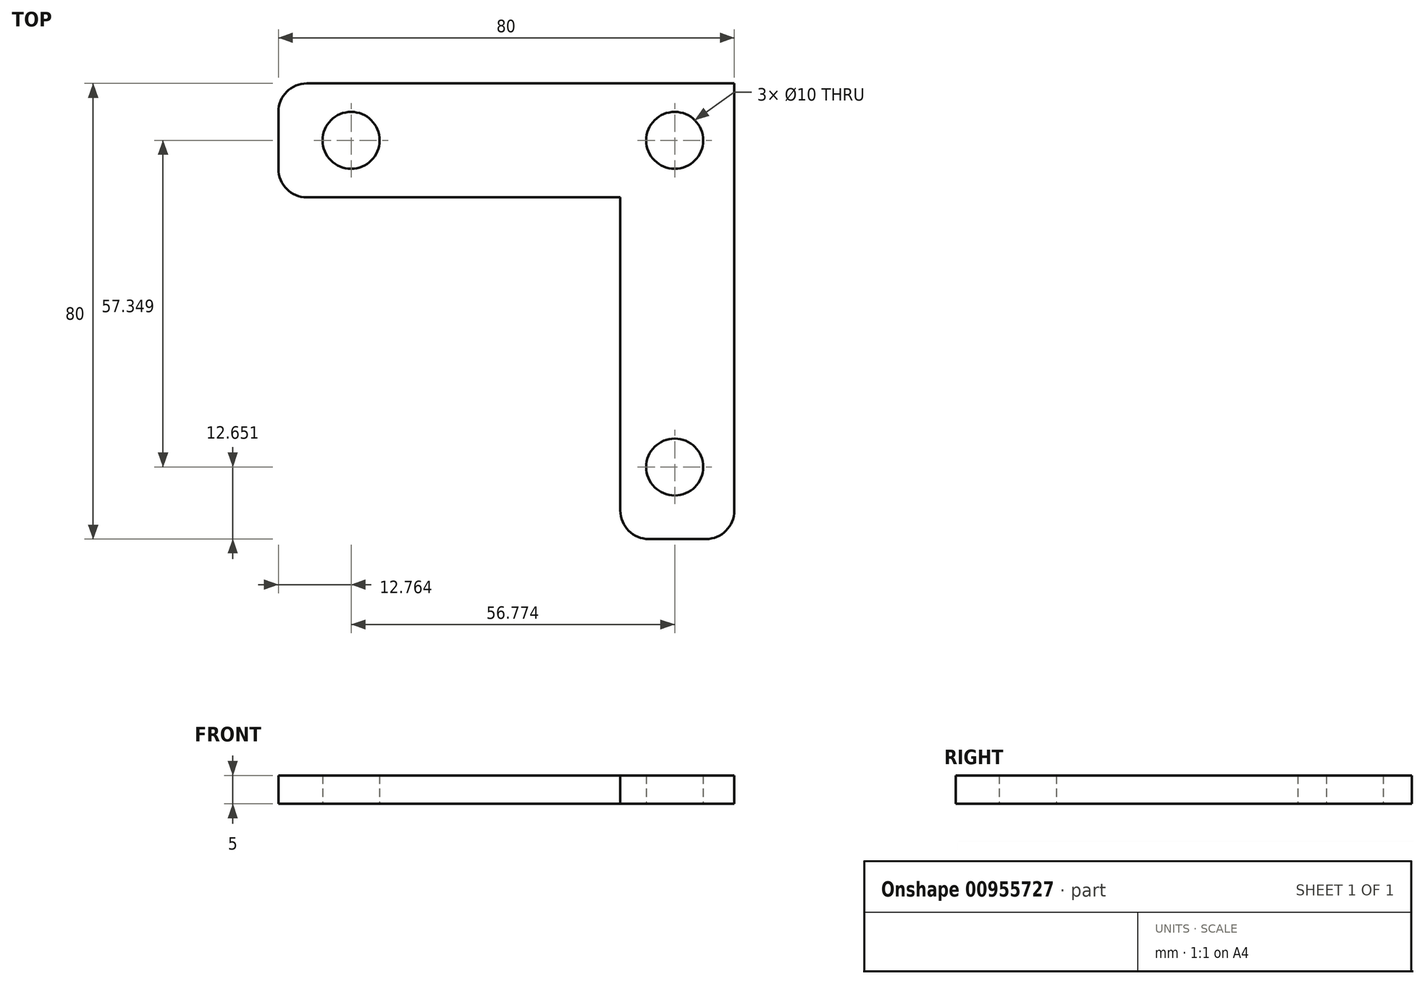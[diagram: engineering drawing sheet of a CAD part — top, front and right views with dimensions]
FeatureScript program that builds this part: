
annotation { "Feature Type Name" : "Feature", "Feature Type Description" : "" }
export const myFeature = defineFeature(function(context is Context, id is Id, definition is map)
    precondition{}
    {
        {
            var Q0;
            Q0=qCreatedBy(makeId("Top.planeOp"),FACE);
            var sketch = newSketch(context, id + "F0", { "sketchPlane" : qUnion([Q0])});
            skLineSegment(sketch, "E0.bottom", {"start": v(40, -10) * mm, "end": v(-40, -10) * mm});
            skLineSegment(sketch, "E0.top", {"start": v(40, 10) * mm, "end": v(-40, 10) * mm});
            skLineSegment(sketch, "E0.left", {"start": v(40, -10) * mm, "end": v(40, 10) * mm});
            skLineSegment(sketch, "E0.right", {"start": v(-40, -10) * mm, "end": v(-40, 10) * mm});
            skPoint(sketch, "E0.middle", {"position": v(0, 0) * mm});
            skLineSegment(sketch, "E1.bottom", {"start": v(40, 10) * mm, "end": v(20, 10) * mm});
            skLineSegment(sketch, "E1.top", {"start": v(40, -70) * mm, "end": v(20, -70) * mm});
            skLineSegment(sketch, "E1.left", {"start": v(40, 10) * mm, "end": v(40, -70) * mm});
            skLineSegment(sketch, "E1.right", {"start": v(20, 10) * mm, "end": v(20, -70) * mm});
            skCircle(sketch, "E2", {"center": v(-27.24, 0) * mm, "radius": 5 * mm});
            skPoint(sketch, "E2.centerSnap0", {"position": v(-40, 0) * mm});
            skCircle(sketch, "E3", {"center": v(29.54, -57.35) * mm, "radius": 5 * mm});
            skCircle(sketch, "E4", {"center": v(29.54, 0) * mm, "radius": 5 * mm});
            skSolve(sketch);
        }
        {
            var Q0;
            {var subQ1=sQuery(id+"F0.wireOp",EDGE,"E0.top");Q0=makeQuery(id+"F0.imprint","IMPRINT",FACE,{"disambiguationData":[TD([[makeQuery(id+"F0.imprint","IMPRINT",EDGE,{"derivedFrom":subQ1}),1.0]])]});}
            var Q1;
            {var subQ1=sQuery(id+"F0.wireOp",EDGE,"E1.top");Q1=makeQuery(id+"F0.imprint","IMPRINT",FACE,{"disambiguationData":[TD([[makeQuery(id+"F0.imprint","IMPRINT",EDGE,{"derivedFrom":subQ1}),-1.0]])]});}
            var Q2;
            {var subQ1=sQuery(id+"F0.wireOp",EDGE,"E1.bottom");Q2=makeQuery(id+"F0.imprint","IMPRINT",FACE,{"disambiguationData":[TD([[makeQuery(id+"F0.imprint","IMPRINT",EDGE,{"derivedFrom":subQ1}),1.0]])]});}
            extrude(context, id + "F1", {"entities" : qUnion([Q0, Q1, Q2]), "depth" : 5 * mm, "offsetDistance" : 25 * mm});
        }
        {
            var Q0;
            Q0=makeQuery(id+"F1.opExtrude","SWEPT_EDGE",EDGE,{"disambiguationData":[OSD([sQuery(id+"F0.wireOp",EDGE,"E1.top"),sQuery(id+"F0.wireOp",EDGE,"E1.right")])]});
            var Q1;
            Q1=makeQuery(id+"F1.opExtrude","SWEPT_EDGE",EDGE,{"disambiguationData":[OSD([sQuery(id+"F0.wireOp",EDGE,"E1.top"),sQuery(id+"F0.wireOp",EDGE,"E1.left")])]});
            var Q2;
            Q2=makeQuery(id+"F1.opExtrude","SWEPT_EDGE",EDGE,{"disambiguationData":[OSD([sQuery(id+"F0.wireOp",EDGE,"E1.bottom"),sQuery(id+"F0.wireOp",EDGE,"E1.left")])]});
            var Q3;
            Q3=makeQuery(id+"F1.opExtrude","SWEPT_EDGE",EDGE,{"disambiguationData":[OSD([sQuery(id+"F0.wireOp",EDGE,"E0.bottom"),sQuery(id+"F0.wireOp",EDGE,"E0.right")])]});
            var Q4;
            Q4=makeQuery(id+"F1.opExtrude","SWEPT_EDGE",EDGE,{"disambiguationData":[OSD([sQuery(id+"F0.wireOp",EDGE,"E0.top"),sQuery(id+"F0.wireOp",EDGE,"E0.right")])]});
            fillet(context, id + "F2", {"entities" : qUnion([Q0, Q1, Q2, Q3, Q4]), "radius" : 5 * mm, "tangentPropagation" : true, "allowEdgeOverflow" : false});
        }
    });
